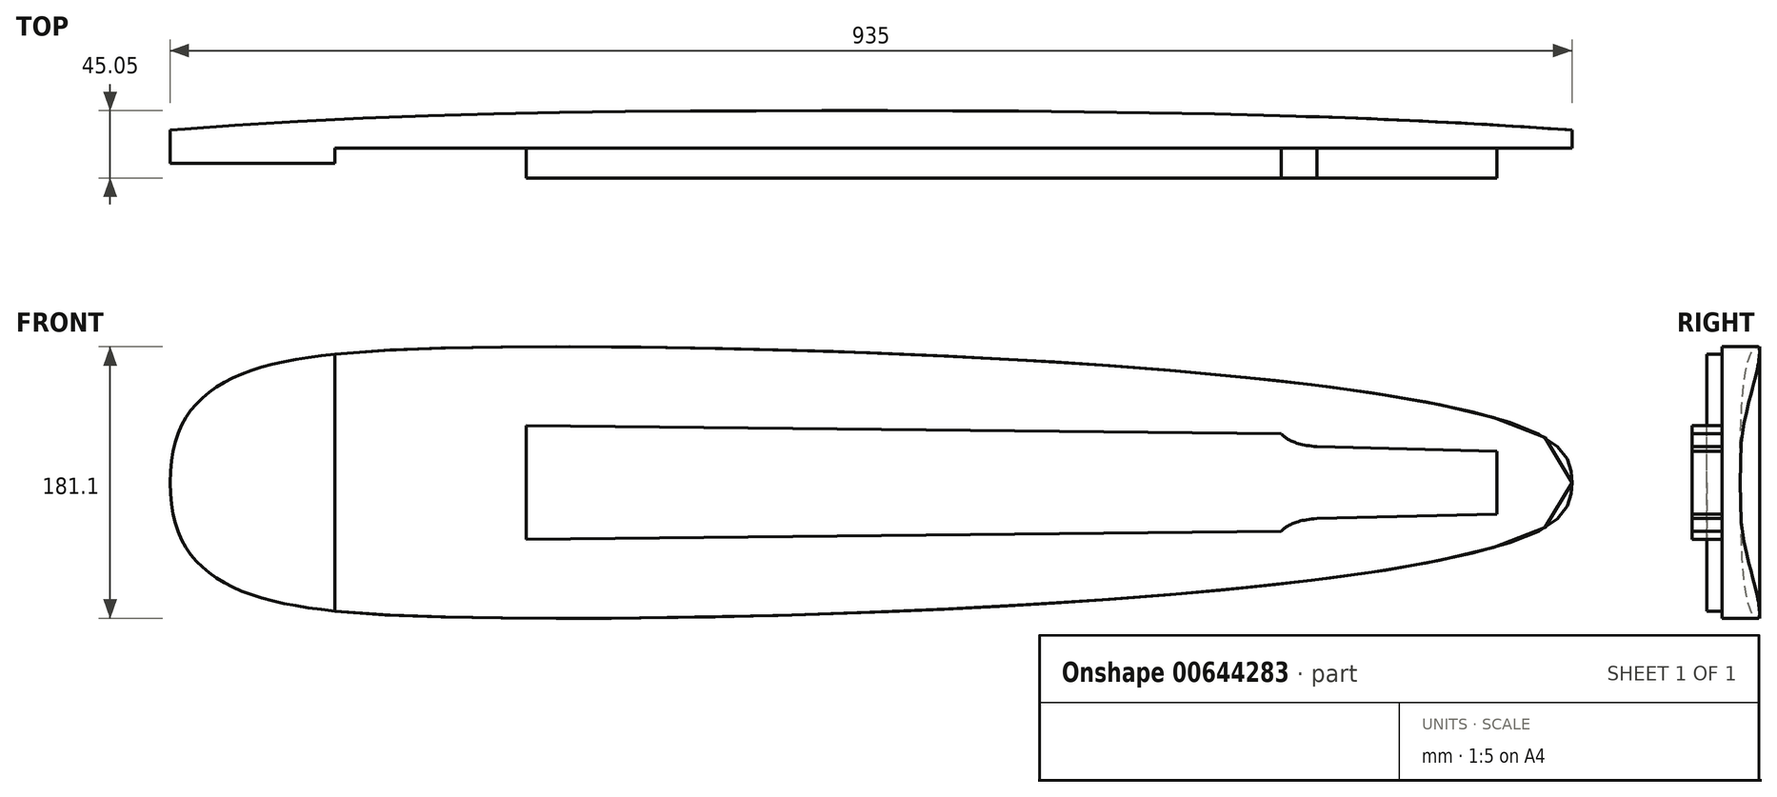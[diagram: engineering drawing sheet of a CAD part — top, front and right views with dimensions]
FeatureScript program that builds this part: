
annotation { "Feature Type Name" : "Feature", "Feature Type Description" : "" }
export const myFeature = defineFeature(function(context is Context, id is Id, definition is map)
    precondition{}
    {
        {
            var Q0;
            Q0=qCreatedBy(makeId("Front.planeOp"),FACE);
            var sketch = newSketch(context, id + "F0", { "sketchPlane" : qUnion([Q0])});
            skLineSegment(sketch, "E0", {"start": v(-433.34, 0) * mm, "end": v(585.98, 0) * mm, "construction": true});
            skLineSegment(sketch, "E1", {"start": v(-325, 152.84) * mm, "end": v(-325, -152.84) * mm, "construction": true});
            skPoint(sketch, "E2", {"position": v(-325, 0) * mm});
            skLineSegment(sketch, "E3", {"start": v(325, 164.83) * mm, "end": v(325, -164.83) * mm, "construction": true});
            skLineSegment(sketch, "E4", {"start": v(0, 164.83) * mm, "end": v(0, -164.83) * mm, "construction": true});
            skPoint(sketch, "E5", {"position": v(0, 0) * mm});
            skLineSegment(sketch, "E6", {"start": v(-385.01, 90) * mm, "end": v(-76.98, 90) * mm, "construction": true});
            skLineSegment(sketch, "E7", {"start": v(-410, 111.2) * mm, "end": v(-410, -121.43) * mm, "construction": true});
            skLineSegment(sketch, "E8", {"start": v(-325, 27) * mm, "end": v(325, 27) * mm, "construction": true});
            skLineSegment(sketch, "E9.MirrorCS", {"start": v(-325, -27) * mm, "end": v(325, -27) * mm, "construction": true});
            skPoint(sketch, "E10.middle", {"position": v(-349.22, 0) * mm});
            skLineSegment(sketch, "E11.MirrorCS", {"start": v(-162.5, -35) * mm, "end": v(-162.5, 0) * mm});
            skLineSegment(sketch, "E12", {"start": v(525, 48.47) * mm, "end": v(525, -48.47) * mm, "construction": true});
            skPoint(sketch, "E13", {"position": v(525, 0) * mm});
            skFitSpline(sketch, "E14", {"points": [v(-410, 0) * mm, v(-212.5, 90) * mm, v(506.89, 30.15) * mm, v(525, 0) * mm], "startDerivative": vector(0, 764.36) * mm, "endDerivative": vector(0, -205.4) * mm});
            skFitSpline(sketch, "E15.MirrorCS", {"points": [v(-410, 0) * mm, v(-212.5, -90) * mm, v(506.89, -30.15) * mm, v(525, 0) * mm], "startDerivative": vector(0, -764.36) * mm, "endDerivative": vector(0, 205.4) * mm});
            skSolve(sketch);
        }
        {
            var Q0;
            Q0=makeQuery(id+"F0.imprint","IMPRINT",FACE,{"disambiguationData":[TD([[makeQuery(id+"F0.imprint","IMPRINT",EDGE,{"derivedFrom":sQuery(id+"F0.wireOp",EDGE,"E14")}),-1.0]])]});
            extrude(context, id + "F1", {"entities" : qUnion([Q0]), "oppositeDirection" : true, "depth" : 30 * mm, "offsetDistance" : 25 * mm});
        }
        {
            var Q0;
            Q0=qCreatedBy(makeId("Top.planeOp"),FACE);
            var sketch = newSketch(context, id + "F2", { "sketchPlane" : qUnion([Q0])});
            skLineSegment(sketch, "E16", {"start": v(-410, 0) * mm, "end": v(-410, 12) * mm});
            skLineSegment(sketch, "E17", {"start": v(525, 0) * mm, "end": v(525, 12) * mm});
            skFitSpline(sketch, "E18", {"points": [v(-410, 12) * mm, v(0, 25) * mm, v(525, 12) * mm], "startDerivative": vector(934.39, 74.63) * mm, "endDerivative": vector(935.61, -70.9) * mm});
            skLineSegment(sketch, "E19", {"start": v(-410, 12) * mm, "end": v(-410, 37) * mm});
            skLineSegment(sketch, "E20", {"start": v(-410, 37) * mm, "end": v(545, 37) * mm});
            skLineSegment(sketch, "E21", {"start": v(545, 37) * mm, "end": v(545, 12) * mm});
            skLineSegment(sketch, "E22", {"start": v(545, 12) * mm, "end": v(525, 12) * mm});
            skSolve(sketch);
        }
        {
            var Q0;
            Q0 = qSketchRegion(id + "F2", true);
            extrude(context, id + "F3", {"entities" : qUnion([Q0]), "operationType" : NewBodyOperationType.REMOVE, "endBound" : BoundingType.SYMMETRIC, "depth" : 1000 * mm, "offsetDistance" : 25 * mm});
        }
        {
            var Q0;
            Q0=makeQuery(id+"F0.imprint","IMPRINT",FACE,{"disambiguationData":[TD([[makeQuery(id+"F0.imprint","IMPRINT",EDGE,{"derivedFrom":sQuery(id+"F0.wireOp",EDGE,"E14")}),-1.0]])]});
            extrude(context, id + "F4", {"entities" : qUnion([Q0]), "operationType" : NewBodyOperationType.ADD, "depth" : 10 * mm, "offsetDistance" : 25 * mm});
        }
        {
            var Q0;
            Q0=makeQuery(id+"F4.opExtrude","CAP_FACE",FACE,{"disambiguationData":[OSD([sQuery(id+"F0.wireOp",EDGE,"E14"),sQuery(id+"F0.wireOp",EDGE,"E15.MirrorCS")])],"isStart":false});
            var sketch = newSketch(context, id + "F5", { "sketchPlane" : qUnion([Q0])});
            skLineSegment(sketch, "E23", {"start": v(-300, 85.77) * mm, "end": v(-300, -85.77) * mm});
            skLineSegment(sketch, "E24", {"start": v(-300, 85.77) * mm, "end": v(-300, 140.85) * mm});
            skLineSegment(sketch, "E25", {"start": v(-300, 140.85) * mm, "end": v(565.54, 140.85) * mm});
            skLineSegment(sketch, "E26", {"start": v(565.54, 140.85) * mm, "end": v(565.54, -145.75) * mm});
            skLineSegment(sketch, "E27", {"start": v(565.54, -145.75) * mm, "end": v(-300, -145.75) * mm});
            skLineSegment(sketch, "E28", {"start": v(-300, -145.75) * mm, "end": v(-300, -122.7) * mm});
            skLineSegment(sketch, "E29", {"start": v(-300, -122.7) * mm, "end": v(-300, -85.77) * mm});
            skSolve(sketch);
        }
        {
            var Q0;
            Q0 = qSketchRegion(id + "F5", true);
            extrude(context, id + "F6", {"entities" : qUnion([Q0]), "operationType" : NewBodyOperationType.REMOVE, "oppositeDirection" : true, "depth" : 10 * mm, "offsetDistance" : 25 * mm});
        }
        {
            var Q0;
            Q0=makeQuery(id+"F0.imprint","IMPRINT",FACE,{"disambiguationData":[TD([[makeQuery(id+"F0.imprint","IMPRINT",EDGE,{"derivedFrom":sQuery(id+"F0.wireOp",EDGE,"E14")}),-1.0]])]});
            var sketch = newSketch(context, id + "F7", { "sketchPlane" : qUnion([Q0])});
            skLineSegment(sketch, "E30", {"start": v(-172.5, 0) * mm, "end": v(-172.5, 38) * mm});
            skLineSegment(sketch, "E31", {"start": v(-172.5, 38) * mm, "end": v(331, 32.56) * mm});
            skLineSegment(sketch, "E32", {"start": v(475, 21) * mm, "end": v(475, 0) * mm});
            skLineSegment(sketch, "E33.MirrorCS", {"start": v(-172.5, -38) * mm, "end": v(331, -32.56) * mm});
            skLineSegment(sketch, "E34.MirrorCS", {"start": v(-172.5, 0) * mm, "end": v(-172.5, -38) * mm});
            skLineSegment(sketch, "E35.MirrorCS", {"start": v(475, -21) * mm, "end": v(475, 0) * mm});
            skLineSegment(sketch, "E36", {"start": v(315.77, 27) * mm, "end": v(359.32, 27) * mm, "construction": true});
            skLineSegment(sketch, "E37", {"start": v(315.77, 16.2) * mm, "end": v(396.68, 16.2) * mm, "construction": true});
            skLineSegment(sketch, "E38", {"start": v(315.77, 5.4) * mm, "end": v(450.23, 5.4) * mm, "construction": true});
            skLineSegment(sketch, "E39.MirrorCS", {"start": v(315.77, -5.4) * mm, "end": v(450.23, -5.4) * mm, "construction": true});
            skLineSegment(sketch, "E40.MirrorCS", {"start": v(315.77, -16.2) * mm, "end": v(396.68, -16.2) * mm, "construction": true});
            skLineSegment(sketch, "E41.MirrorCS", {"start": v(315.77, -27) * mm, "end": v(359.32, -27) * mm, "construction": true});
            skLineSegment(sketch, "E42", {"start": v(358.29, 23.92) * mm, "end": v(471.75, 21.08) * mm, "construction": true});
            skLineSegment(sketch, "E43", {"start": v(415.02, 22.5) * mm, "end": v(414.36, -4) * mm, "construction": true});
            skLineSegment(sketch, "E44", {"start": v(450, 21.63) * mm, "end": v(449.35, -4.87) * mm, "construction": true});
            skLineSegment(sketch, "E45", {"start": v(380.03, 23.38) * mm, "end": v(379.37, -3.12) * mm, "construction": true});
            skPoint(sketch, "E46", {"position": v(415.02, 22.5) * mm});
            skLineSegment(sketch, "E47.MirrorCS", {"start": v(358.29, -23.92) * mm, "end": v(471.75, -21.08) * mm, "construction": true});
            skLineSegment(sketch, "E48.MirrorCS", {"start": v(380.03, -23.38) * mm, "end": v(379.37, 3.12) * mm, "construction": true});
            skLineSegment(sketch, "E49.MirrorCS", {"start": v(415.02, -22.5) * mm, "end": v(414.36, 4) * mm, "construction": true});
            skLineSegment(sketch, "E50.MirrorCS", {"start": v(450, -21.63) * mm, "end": v(449.35, 4.87) * mm, "construction": true});
            skLineSegment(sketch, "E51", {"start": v(331, 32.56) * mm, "end": v(331, -32.56) * mm, "construction": true});
            skLineSegment(sketch, "E52", {"start": v(355.04, 24) * mm, "end": v(475, 21) * mm});
            skLineSegment(sketch, "E53.MirrorCS", {"start": v(355.04, -24) * mm, "end": v(475, -21) * mm});
            skFitSpline(sketch, "E54", {"points": [v(331, 32.56) * mm, v(355.04, 24) * mm], "startDerivative": vector(10.13, -10.54) * mm, "endDerivative": vector(44.63, -3.07) * mm});
            skFitSpline(sketch, "E55.MirrorCS", {"points": [v(331, -32.56) * mm, v(355.04, -24) * mm], "startDerivative": vector(10.13, 10.54) * mm, "endDerivative": vector(44.63, 3.07) * mm});
            skPoint(sketch, "E56.orphan", {"position": v(475, 31) * mm});
            skPoint(sketch, "E57.orphan", {"position": v(475, -31) * mm});
            skSolve(sketch);
        }
        {
            var Q0;
            Q0 = qSketchRegion(id + "F7", true);
            extrude(context, id + "F8", {"entities" : qUnion([Q0]), "operationType" : NewBodyOperationType.ADD, "depth" : 20 * mm, "offsetDistance" : 25 * mm});
        }
    });
